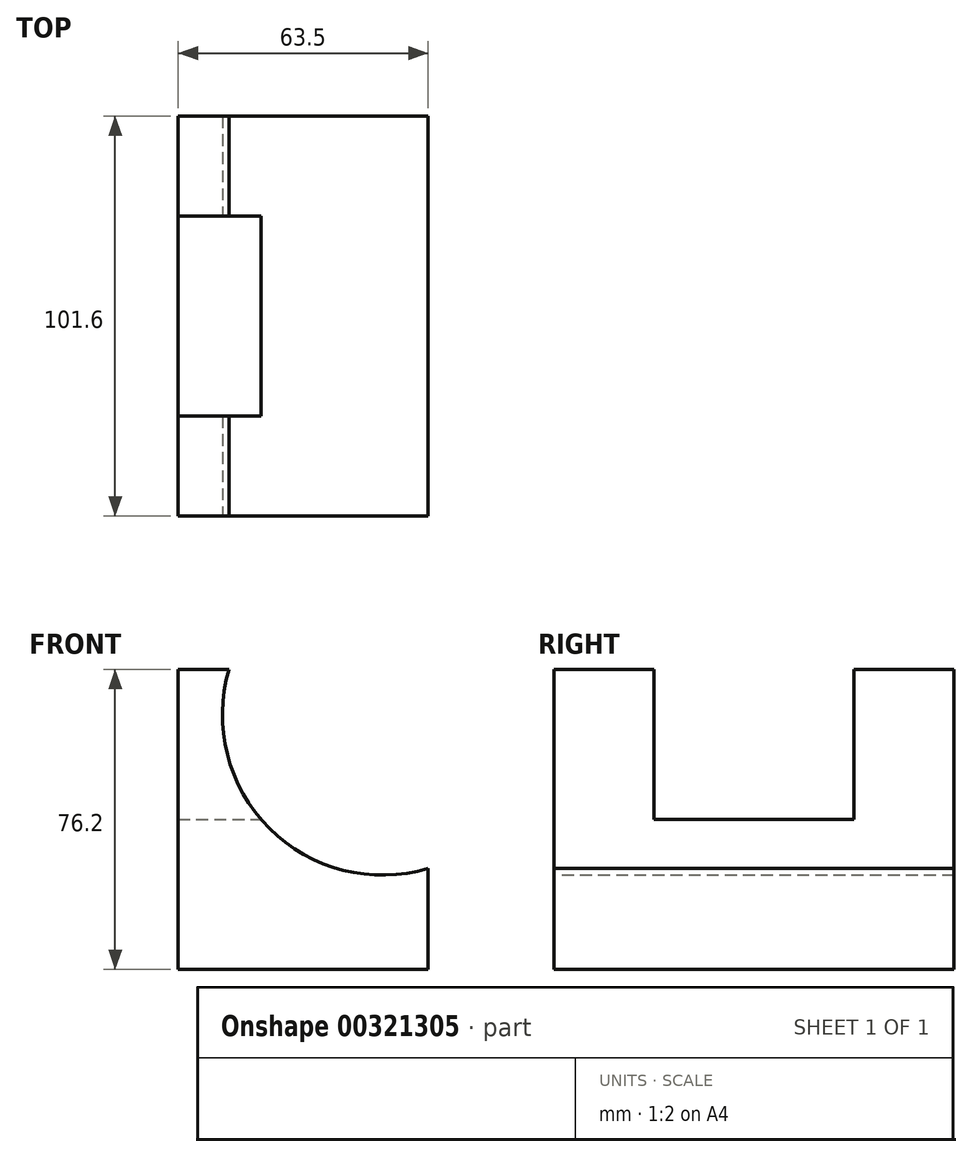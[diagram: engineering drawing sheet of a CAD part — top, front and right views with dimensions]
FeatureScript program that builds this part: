
annotation { "Feature Type Name" : "Feature", "Feature Type Description" : "" }
export const myFeature = defineFeature(function(context is Context, id is Id, definition is map)
    precondition{}
    {
        {
            var Q0;
            Q0=qCreatedBy(makeId("Front.planeOp"),FACE);
            var sketch = newSketch(context, id + "F0", { "sketchPlane" : qUnion([Q0])});
            skLineSegment(sketch, "E0", {"start": v(-51.92, 39.94) * mm, "end": v(-51.92, -36.26) * mm});
            skLineSegment(sketch, "E1", {"start": v(-51.92, -36.26) * mm, "end": v(11.58, -36.26) * mm});
            skLineSegment(sketch, "E2", {"start": v(-51.92, 39.94) * mm, "end": v(11.58, 39.94) * mm});
            skLineSegment(sketch, "E3", {"start": v(11.58, 39.94) * mm, "end": v(11.58, -36.26) * mm});
            skSolve(sketch);
        }
        {
            var Q0;
            Q0 = qSketchRegion(id + "F0", true);
            extrude(context, id + "F1", {"entities" : qUnion([Q0]), "depth" : 101.6 * mm});
        }
        {
            var Q0;
            Q0=makeQuery(id+"F1.opExtrude","CAP_FACE",FACE,{"disambiguationData":[OSD([sQuery(id+"F0.wireOp",EDGE,"E0"),sQuery(id+"F0.wireOp",EDGE,"E1"),sQuery(id+"F0.wireOp",EDGE,"E2"),sQuery(id+"F0.wireOp",EDGE,"E3")])],"isStart":false});
            var sketch = newSketch(context, id + "F2", { "sketchPlane" : qUnion([Q0])});
            skCircle(sketch, "E4", {"center": v(0, 28.37) * mm, "radius": 40.69 * mm});
            skLineSegment(sketch, "E5", {"start": v(-39.22, 39.94) * mm, "end": v(11.58, 39.94) * mm});
            skLineSegment(sketch, "E6", {"start": v(11.58, 39.94) * mm, "end": v(11.58, -10.86) * mm});
            skSolve(sketch);
        }
        {
            var Q0;
            Q0 = qSketchRegion(id + "F2", true);
            extrude(context, id + "F3", {"entities" : qUnion([Q0]), "operationType" : NewBodyOperationType.REMOVE, "oppositeDirection" : true, "depth" : 144.02 * mm});
        }
        {
            var Q0;
            Q0=makeQuery(id+"F1.opExtrude","SWEPT_FACE",FACE,{"disambiguationData":[OSD([sQuery(id+"F0.wireOp",EDGE,"E2")])]});
            var sketch = newSketch(context, id + "F4", { "sketchPlane" : qUnion([Q0])});
            skLineSegment(sketch, "E7", {"start": v(-51.92, -101.6) * mm, "end": v(-51.92, -76.2) * mm});
            skLineSegment(sketch, "E8", {"start": v(-51.92, 0) * mm, "end": v(-51.92, -25.4) * mm});
            skLineSegment(sketch, "E9", {"start": v(-51.92, -76.2) * mm, "end": v(-26.52, -76.2) * mm});
            skLineSegment(sketch, "E10", {"start": v(-51.92, -25.4) * mm, "end": v(-26.52, -25.4) * mm});
            skLineSegment(sketch, "E11", {"start": v(-26.52, -25.4) * mm, "end": v(-26.52, -76.2) * mm});
            skSolve(sketch);
        }
        {
            var Q0;
            {var subQ0=sQuery(id+"F4.wireOp",EDGE,"E11");Q0=makeQuery(id+"F4.imprint","IMPRINT",FACE,{"disambiguationData":[TD([[makeQuery(id+"F4.imprint","IMPRINT",EDGE,{"derivedFrom":subQ0}),-1.0]])]});}
            var Q1;
            {var subQ0=sQuery(id+"F4.wireOp",EDGE,"E9");var subQ1=sQuery(id+"F0.wireOp",EDGE,"E2");var subQ4=makeQuery(id+"F3.boolean.opBoolean","INTERSECT",EDGE,{"derivedFrom":[makeQuery(id+"F1.opExtrude","SWEPT_FACE",FACE,{"disambiguationData":[OSD([subQ1])]}),makeQuery(id+"F3.opExtrude","SWEPT_FACE",FACE,{"disambiguationData":[OSD([sQuery(id+"F2.wireOp",EDGE,"E4")])]})]});var subQ5=makeQuery(id+"F4.imprint","INTERSECT",VERTEX,{"derivedFrom":[subQ4,subQ0]});Q1=makeQuery(id+"F4.imprint","IMPRINT",FACE,{"disambiguationData":[TD([[makeQuery(id+"F4.imprint","IMPRINT",EDGE,{"disambiguationData":[TD([[subQ5,1.0]])],"derivedFrom":subQ0}),1.0]])]});}
            extrude(context, id + "F5", {"entities" : qUnion([Q0, Q1]), "operationType" : NewBodyOperationType.REMOVE, "oppositeDirection" : true, "depth" : 38.1 * mm});
        }
    });
